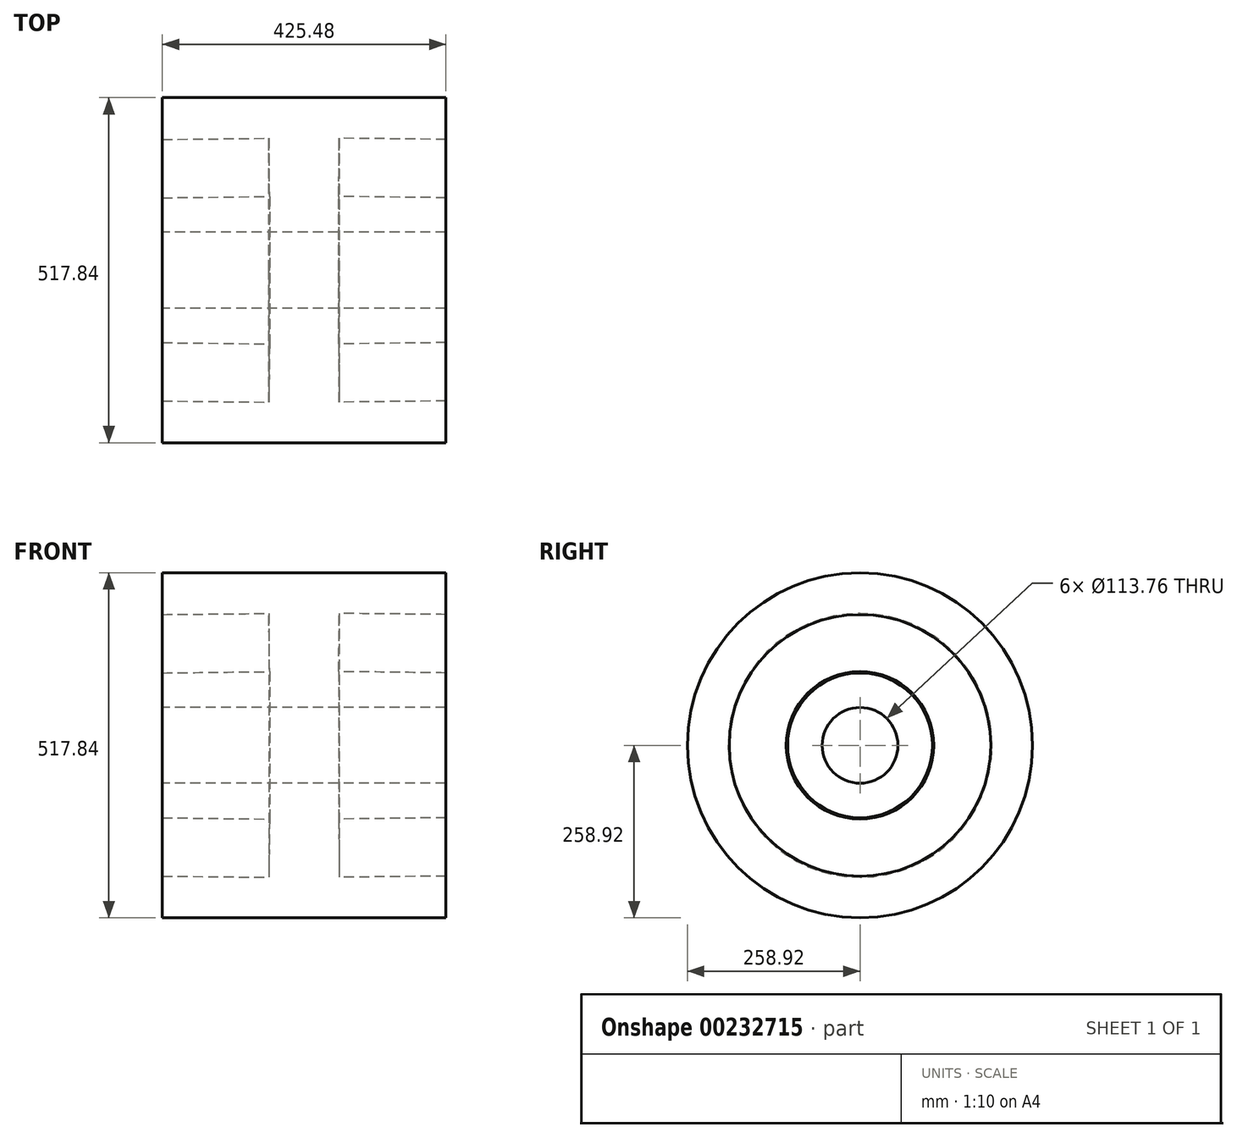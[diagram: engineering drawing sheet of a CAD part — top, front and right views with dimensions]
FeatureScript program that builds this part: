
annotation { "Feature Type Name" : "Feature", "Feature Type Description" : "" }
export const myFeature = defineFeature(function(context is Context, id is Id, definition is map)
    precondition{}
    {
        {
            var Q0;
            Q0=qCreatedBy(makeId("Front.planeOp"),FACE);
            var sketch = newSketch(context, id + "F0", { "sketchPlane" : qUnion([Q0])});
            skLineSegment(sketch, "E0", {"start": v(-182.02, 0) * mm, "end": v(212.3, 0) * mm, "construction": true});
            skLineSegment(sketch, "E1", {"start": v(0, 0) * mm, "end": v(0, 340.07) * mm, "construction": true});
            skLineSegment(sketch, "E2", {"start": v(0, 258.92) * mm, "end": v(212.74, 258.92) * mm});
            skLineSegment(sketch, "E3", {"start": v(212.74, 258.92) * mm, "end": v(212.74, 196.28) * mm});
            skLineSegment(sketch, "E4", {"start": v(212.74, 196.28) * mm, "end": v(52.87, 197.88) * mm});
            skLineSegment(sketch, "E5", {"start": v(52.87, 197.88) * mm, "end": v(51.78, 110.65) * mm});
            skLineSegment(sketch, "E6", {"start": v(51.78, 110.65) * mm, "end": v(212.74, 108.64) * mm});
            skLineSegment(sketch, "E7", {"start": v(212.74, 108.64) * mm, "end": v(212.3, 56.88) * mm});
            skLineSegment(sketch, "E8", {"start": v(212.3, 56.88) * mm, "end": v(0, 56.88) * mm});
            skLineSegment(sketch, "E9.MirrorCS", {"start": v(0, 258.92) * mm, "end": v(-212.74, 258.92) * mm});
            skLineSegment(sketch, "E10.MirrorCS", {"start": v(-212.74, 258.92) * mm, "end": v(-212.74, 196.28) * mm});
            skLineSegment(sketch, "E11.MirrorCS", {"start": v(-212.74, 196.28) * mm, "end": v(-52.87, 197.88) * mm});
            skLineSegment(sketch, "E12.MirrorCS", {"start": v(-52.87, 197.88) * mm, "end": v(-51.78, 110.65) * mm});
            skLineSegment(sketch, "E13.MirrorCS", {"start": v(-51.78, 110.65) * mm, "end": v(-212.74, 108.64) * mm});
            skLineSegment(sketch, "E14.MirrorCS", {"start": v(-212.3, 56.88) * mm, "end": v(0, 56.88) * mm});
            skLineSegment(sketch, "E15.MirrorCS", {"start": v(-212.74, 108.64) * mm, "end": v(-212.3, 56.88) * mm});
            skSolve(sketch);
        }
        {
            var Q0;
            Q0=makeQuery(id+"F0.imprint","IMPRINT",FACE,{"disambiguationData":[TD([[makeQuery(id+"F0.imprint","IMPRINT",EDGE,{"derivedFrom":sQuery(id+"F0.wireOp",EDGE,"E2")}),-1.0]])]});
            var Q1;
            Q1=sQuery(id+"F0.wireOp",EDGE,"E0");
            revolve(context, id + "F1", {"entities" : qUnion([Q0]), "axis" : qUnion([Q1]), "revolveType" : RevolveType.FULL});
        }
    });
